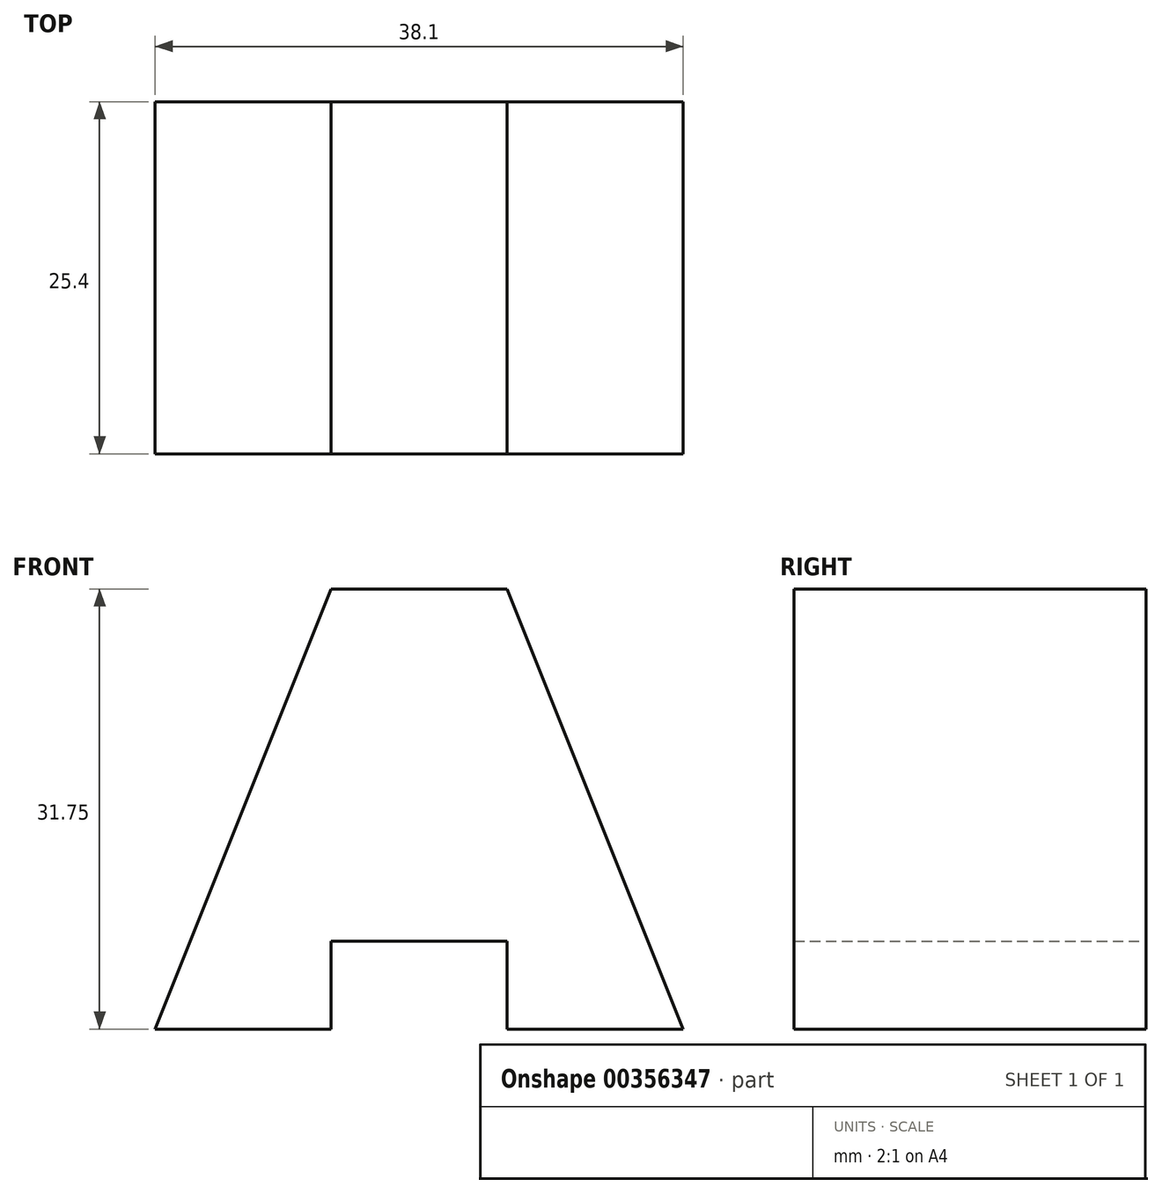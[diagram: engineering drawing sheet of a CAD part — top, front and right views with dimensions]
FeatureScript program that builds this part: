
annotation { "Feature Type Name" : "Feature", "Feature Type Description" : "" }
export const myFeature = defineFeature(function(context is Context, id is Id, definition is map)
    precondition{}
    {
        {
            var Q0;
            Q0=qCreatedBy(makeId("Front.planeOp"),FACE);
            var sketch = newSketch(context, id + "F0", { "sketchPlane" : qUnion([Q0])});
            skLineSegment(sketch, "E0", {"start": v(0, 0) * mm, "end": v(38.1, 0) * mm});
            skLineSegment(sketch, "E1", {"start": v(38.1, 0) * mm, "end": v(38.1, 31.75) * mm});
            skLineSegment(sketch, "E2", {"start": v(38.1, 31.75) * mm, "end": v(0, 31.75) * mm});
            skLineSegment(sketch, "E3", {"start": v(0, 31.75) * mm, "end": v(0, 0) * mm});
            skLineSegment(sketch, "E4", {"start": v(12.7, 0) * mm, "end": v(12.7, 6.35) * mm});
            skLineSegment(sketch, "E5", {"start": v(12.7, 6.35) * mm, "end": v(25.4, 6.35) * mm});
            skLineSegment(sketch, "E6", {"start": v(25.4, 6.35) * mm, "end": v(25.4, 0) * mm});
            skSolve(sketch);
        }
        {
            var Q0;
            {var subQ0=sQuery(id+"F0.wireOp",EDGE,"E1");Q0=makeQuery(id+"F0.imprint","IMPRINT",FACE,{"disambiguationData":[TD([[makeQuery(id+"F0.imprint","IMPRINT",EDGE,{"derivedFrom":subQ0}),1.0]])]});}
            extrude(context, id + "F1", {"entities" : qUnion([Q0]), "depth" : 25.4 * mm});
        }
        {
            var Q0;
            Q0=makeQuery(id+"F1.opExtrude","CAP_FACE",FACE,{"disambiguationData":[OSD([sQuery(id+"F0.wireOp",EDGE,"E0"),sQuery(id+"F0.wireOp",EDGE,"E1"),sQuery(id+"F0.wireOp",EDGE,"E2"),sQuery(id+"F0.wireOp",EDGE,"E3"),sQuery(id+"F0.wireOp",EDGE,"E4"),sQuery(id+"F0.wireOp",EDGE,"E5"),sQuery(id+"F0.wireOp",EDGE,"E6")])],"isStart":false});
            var sketch = newSketch(context, id + "F2", { "sketchPlane" : qUnion([Q0])});
            skLineSegment(sketch, "E7", {"start": v(12.7, 31.75) * mm, "end": v(0, 0) * mm});
            skLineSegment(sketch, "E8", {"start": v(25.4, 31.75) * mm, "end": v(38.1, 0) * mm});
            skSolve(sketch);
        }
        {
            var Q0;
            {var subQ0=sQuery(id+"F2.wireOp",EDGE,"E8");Q0=makeQuery(id+"F2.imprint","IMPRINT",FACE,{"disambiguationData":[TD([[makeQuery(id+"F2.imprint","IMPRINT",EDGE,{"derivedFrom":subQ0}),1.0]])]});}
            extrude(context, id + "F3", {"entities" : qUnion([Q0]), "operationType" : NewBodyOperationType.REMOVE, "oppositeDirection" : true, "depth" : 25.4 * mm});
        }
        {
            var Q0;
            Q0=makeQuery(id+"F1.opExtrude","CAP_FACE",FACE,{"disambiguationData":[OSD([sQuery(id+"F0.wireOp",EDGE,"E0"),sQuery(id+"F0.wireOp",EDGE,"E1"),sQuery(id+"F0.wireOp",EDGE,"E2"),sQuery(id+"F0.wireOp",EDGE,"E3"),sQuery(id+"F0.wireOp",EDGE,"E4"),sQuery(id+"F0.wireOp",EDGE,"E5"),sQuery(id+"F0.wireOp",EDGE,"E6")])],"isStart":false});
            var sketch = newSketch(context, id + "F4", { "sketchPlane" : qUnion([Q0])});
            skLineSegment(sketch, "E9", {"start": v(12.7, 31.75) * mm, "end": v(0, 0) * mm});
            skSolve(sketch);
        }
        {
            var Q0;
            {var subQ0=sQuery(id+"F4.wireOp",EDGE,"E9");Q0=makeQuery(id+"F4.imprint","IMPRINT",FACE,{"disambiguationData":[TD([[makeQuery(id+"F4.imprint","IMPRINT",EDGE,{"derivedFrom":subQ0}),-1.0]])]});}
            extrude(context, id + "F5", {"entities" : qUnion([Q0]), "operationType" : NewBodyOperationType.REMOVE, "oppositeDirection" : true, "depth" : 25.4 * mm});
        }
    });
